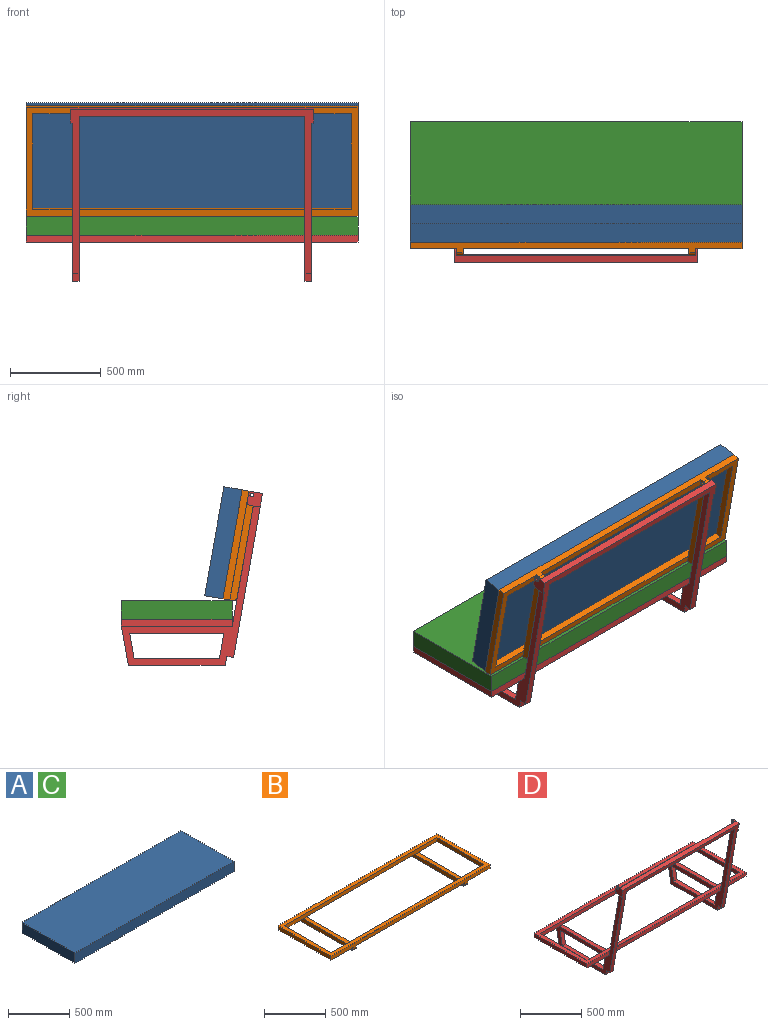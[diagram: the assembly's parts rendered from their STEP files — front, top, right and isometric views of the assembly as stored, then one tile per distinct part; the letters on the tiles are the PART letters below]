
ASSEMBLY  parts=4 mates=5
PART A: 6 faces, bbox 1828.8x609.6x101.6 mm
  f0: plane 609.6x101.6mm, normal (-1,0,0), area 61935.4mm2, adj f1,f3,f4,f5
  f1: plane 1828.8x101.6mm, normal (0,-1,0), area 185806.1mm2, adj f0,f2,f4,f5
  f2: plane 609.6x101.6mm, normal (1,0,0), area 61935.4mm2, adj f1,f3,f4,f5
  f3: plane 1828.8x101.6mm, normal (0,1,0), area 185806.1mm2, adj f0,f2,f4,f5
  f4: plane 1828.8x609.6mm, normal (0,0,1), area 1114836.5mm2, adj f0,f1,f2,f3
  f5: plane 1828.8x609.6mm, normal (0,0,-1), area 1114836.5mm2, adj f0,f1,f2,f3
PART B: 27 faces, bbox 1828.8x609.6x76.2 mm
  f0: plane 1244.6x38.1mm, normal (0,0,-1), area 47419.3mm2, adj f6,f9,f15,f19
  f1: plane 1244.6x38.1mm, normal (0,0,-1), area 47419.3mm2, adj f8,f11,f15,f19
  f2: plane 609.6x254mm, normal (0,0,-1), area 39677.3mm2, adj f5,f6,f8,f9,f10,f11,f16
  f3: plane 609.6x254mm, normal (0,0,-1), area 39677.3mm2, adj f6,f7,f8,f9,f11,f12,f20
  f4: plane 1828.8x609.6mm, normal (0,0,1), area 179999.6mm2, adj f5,f6,f7,f8,f9,f10,f11,f12
  f5: plane 609.6x38.1mm, normal (-1,0,0), area 23225.8mm2, adj f2,f4,f6,f8
  f6: plane 1828.8x57.15mm, normal (0,-1,0), area 71128.9mm2, adj f0,f2,f3,f4,f5,f7,f15,f16
  f7: plane 609.6x38.1mm, normal (1,0,0), area 23225.8mm2, adj f3,f4,f6,f8
  f8: plane 1828.8x57.15mm, normal (0,1,0), area 71128.9mm2, adj f1,f2,f3,f4,f5,f7,f15,f16
  f9: plane 1752.6x38.1mm, normal (0,1,0), area 66774.1mm2, adj f0,f2,f3,f4,f10,f12,f13,f17
  f10: plane 533.4x38.1mm, normal (1,0,0), area 20322.5mm2, adj f2,f4,f9,f11
  f11: plane 1752.6x38.1mm, normal (0,-1,0), area 66774.1mm2, adj f1,f2,f3,f4,f10,f12,f13,f17
  f12: plane 533.4x38.1mm, normal (-1,0,0), area 20322.5mm2, adj f3,f4,f9,f11
  f13: plane 533.4x38.1mm, normal (0,0,1), area 20322.5mm2, adj f9,f11,f15,f16
  f14: plane 571.5x38.1mm, normal (0,0,-1), area 21774.2mm2, adj f15,f16,f25,f26
  f15: plane 609.6x38.1mm, normal (1,0,0), area 22785mm2, adj f0,f1,f6,f8,f13,f14,f22,f25
  f16: plane 609.6x38.1mm, normal (-1,0,0), area 22785mm2, adj f2,f6,f8,f13,f14,f22,f25,f26
  f17: plane 533.4x38.1mm, normal (0,0,1), area 20322.5mm2, adj f9,f11,f19,f20
  f18: plane 571.5x38.1mm, normal (0,0,-1), area 21774.2mm2, adj f19,f20,f23,f24
  f19: plane 609.6x38.1mm, normal (-1,0,0), area 22785mm2, adj f0,f1,f6,f8,f17,f18,f21,f23
  f20: plane 609.6x38.1mm, normal (1,0,0), area 22785mm2, adj f3,f6,f8,f17,f18,f21,f23,f24
  f21: cylinder r=9.53mm len=38.1mm, axis (-1,0,0), area 2280.2mm2, adj f19,f20
  f22: cylinder r=9.53mm len=38.1mm, axis (-1,0,0), area 2280.2mm2, adj f15,f16
  f23: cylinder r=19.05mm len=38.1mm, axis (1,0,0), area 1140.1mm2, adj f8,f18,f19,f20
  f24: cylinder r=19.05mm len=38.1mm, axis (-1,0,0), area 1140.1mm2, adj f6,f18,f19,f20
  f25: cylinder r=19.05mm len=38.1mm, axis (1,0,0), area 1140.1mm2, adj f8,f14,f15,f16
  f26: cylinder r=19.05mm len=38.1mm, axis (-1,0,0), area 1140.1mm2, adj f6,f14,f15,f16
PART C: same geometry as A
PART D: 53 faces, bbox 1828.8x777.1x956.8 mm
  f0: plane 878.2x763.9mm, normal (1,0,0), area 86400.3mm2, adj f5,f25,f26,f27,f28,f29,f30,f31
  f1: plane 915.73x770.52mm, normal (-1,0,0), area 87851.9mm2, adj f2,f3,f25,f26,f27,f28,f29,f30
  f2: plane 1244.6x38.1mm, normal (0,0,-1), area 47419.3mm2, adj f1,f8,f11,f23
  f3: plane 1244.6x38.1mm, normal (0,0,-1), area 47419.3mm2, adj f1,f10,f13,f23
  f4: plane 609.6x254mm, normal (0,0,-1), area 39677.3mm2, adj f7,f8,f10,f11,f12,f13,f24
  f5: plane 609.6x254mm, normal (0,0,-1), area 39677.3mm2, adj f0,f8,f9,f10,f11,f13,f14
  f6: plane 1828.8x609.6mm, normal (0,0,1), area 179999.6mm2, adj f7,f8,f9,f10,f11,f12,f13,f14
  f7: plane 609.6x38.1mm, normal (-1,0,0), area 23225.8mm2, adj f4,f6,f8,f10
  f8: plane 1828.8x38.1mm, normal (0,-1,0), area 69677.3mm2, adj f2,f4,f5,f6,f7,f9,f33
  f9: plane 609.6x38.1mm, normal (1,0,0), area 23225.8mm2, adj f5,f6,f8,f10
  f10: plane 1828.8x38.1mm, normal (0,1,0), area 69677.3mm2, adj f3,f4,f5,f6,f7,f9,f16,f32
  f11: plane 1752.6x38.1mm, normal (0,1,0), area 66774.1mm2, adj f2,f4,f5,f6,f12,f14,f15,f25
  f12: plane 533.4x38.1mm, normal (1,0,0), area 20322.5mm2, adj f4,f6,f11,f13
  f13: plane 1752.6x38.1mm, normal (0,-1,0), area 66774.1mm2, adj f3,f4,f5,f6,f12,f14,f15,f25
  f14: plane 533.4x38.1mm, normal (-1,0,0), area 20322.5mm2, adj f5,f6,f11,f13
  f15: plane 533.4x38.1mm, normal (0,0,1), area 20322.5mm2, adj f11,f13,f23,f24
  f16: plane 215.9x38.1mm, normal (0,0.98,-0.17), area 8352.7mm2, adj f10,f17,f23,f24
  f17: plane 533.46x38.1mm, normal (0,0,-1), area 20324.9mm2, adj f16,f22,f23,f24
  f18: plane 469.52x38.1mm, normal (0,0,1), area 17888.8mm2, adj f19,f21,f23,f24
  f19: plane 139.7x38.1mm, normal (0,-0.98,0.17), area 5404.7mm2, adj f18,f20,f23,f24
  f20: plane 518.79x38.1mm, normal (0,0,-1), area 19765.8mm2, adj f19,f21,f23,f24
  f21: plane 139.7x38.1mm, normal (0,0.98,0.17), area 5404.7mm2, adj f18,f20,f23,f24
  f22: plane 50.03x38.1mm, normal (0,-0.98,-0.17), area 1935.5mm2, adj f17,f23,f24,f34
  f23: plane 915.73x770.52mm, normal (1,0,0), area 87851.9mm2, adj f2,f3,f15,f16,f17,f18,f19,f20
  f24: plane 878.2x763.9mm, normal (-1,0,0), area 86400.3mm2, adj f4,f15,f16,f17,f18,f19,f20,f21
  f25: plane 533.4x38.1mm, normal (0,0,1), area 20322.5mm2, adj f0,f1,f11,f13
  f26: plane 50.03x38.1mm, normal (0,-0.98,-0.17), area 1935.5mm2, adj f0,f1,f27,f37
  f27: plane 533.46x38.1mm, normal (0,0,-1), area 20324.9mm2, adj f0,f1,f26,f32
  f28: plane 469.52x38.1mm, normal (0,0,1), area 17888.8mm2, adj f0,f1,f29,f31
  f29: plane 139.7x38.1mm, normal (0,0.98,0.17), area 5404.7mm2, adj f0,f1,f28,f30
  f30: plane 518.79x38.1mm, normal (0,0,-1), area 19765.8mm2, adj f0,f1,f29,f31
  f31: plane 139.7x38.1mm, normal (0,-0.98,0.17), area 5404.7mm2, adj f0,f1,f28,f30
  f32: plane 215.9x38.1mm, normal (0,0.98,-0.17), area 8352.7mm2, adj f0,f1,f10,f27
  f33: plane 1320.8x737.35mm, normal (0,0.98,0.17), area 104471.8mm2, adj f0,f1,f8,f23,f24,f35,f38,f43
  f34: plane 38.1x37.52mm, normal (0,0.17,-0.98), area 1451.6mm2, adj f22,f23,f24,f36
  f35: plane 1339.85x56.28mm, normal (0,-0.17,0.98), area 51411.2mm2, adj f33,f36,f42,f43,f44,f46,f50,f51
  f36: plane 1339.85x903.22mm, normal (0,-0.98,-0.17), area 118757.8mm2, adj f0,f1,f23,f24,f34,f35,f37,f38
  f37: plane 38.1x37.52mm, normal (0,0.17,-0.98), area 1451.6mm2, adj f0,f1,f26,f36
  f38: plane 1244.6x37.52mm, normal (0,0.17,-0.98), area 47419.3mm2, adj f1,f23,f33,f36
  f39: plane 37.52x9.53mm, normal (0,0.98,0.17), area 362.9mm2, adj f42,f43,f44,f45
  f40: plane 56.28x9.92mm, normal (0,0.17,-0.98), area 544.4mm2, adj f24,f36,f42,f43,f45
  f41: cylinder r=9.53mm len=19.05mm, axis (1,0,0), area 570mm2, adj f42,f43
  f42: plane 85.26x85.26mm, normal (-1,0,0), area 5365.7mm2, adj f35,f36,f39,f40,f41,f44,f45
  f43: plane 78.64x47.73mm, normal (1,0,0), area 2462.4mm2, adj f33,f35,f39,f40,f41,f44,f45
  f44: cylinder r=19.05mm len=22.07mm, axis (-1,0,0), area 285mm2, adj f35,f39,f42,f43
  f45: cylinder r=19.05mm len=22.07mm, axis (1,0,0), area 285mm2, adj f39,f40,f42,f43
  f46: plane 78.64x47.73mm, normal (-1,0,0), area 2462.4mm2, adj f33,f35,f47,f48,f49,f51,f52
  f47: plane 56.28x9.92mm, normal (0,0.17,-0.98), area 544.4mm2, adj f0,f36,f46,f50,f52
  f48: plane 37.52x9.53mm, normal (0,0.98,0.17), area 362.9mm2, adj f46,f50,f51,f52
  f49: cylinder r=9.53mm len=19.05mm, axis (-1,0,0), area 570mm2, adj f46,f50
  f50: plane 85.26x85.26mm, normal (1,0,0), area 5365.7mm2, adj f35,f36,f47,f48,f49,f51,f52
  f51: cylinder r=19.05mm len=22.07mm, axis (-1,0,0), area 285mm2, adj f35,f46,f48,f50
  f52: cylinder r=19.05mm len=22.07mm, axis (-1,0,0), area 285mm2, adj f46,f47,f48,f50
PLACE A rot(axis=(-1,0,0),80deg) t=(0,-54.97,712.48)mm
PLACE B rot(axis=(-1,0,0),80deg) t=(0,-54.97,712.48)mm
PLACE C at identity
PLACE D at identity fixed
MATE revolute B.f21 <-> D.f41  axis (1,0,0) through (1574.8,-107.95,683.79)mm
MATE parallel B.f14 <-> D.f36  axis (0,-0.98,-0.17) through (273.05,-77.09,399.08)mm
MATE fastened A.f5 <-> B.f4  axis (0,0.98,0.17) through (1828.8,-54.97,712.48)mm
MATE planar A.f5 <-> B.f4  axis (0,-0.98,-0.17) through (914.4,-2.04,412.31)mm
MATE fastened C.f5 <-> D.f6  axis (0,0,1) through (1828.8,609.6,0)mm
